# Revit family: BE_24533_de_DE
name_source: partatom
category: Leuchten
units: mm (PartAtom-declared; Revit-internal decimal feet)

## family parameters
Basisbauteil = Fläche
Beim Laden mit Abzugskörper schneiden = Ja
Bemaßung runder Anschluss = Durchmesser verwenden
Gemeinsam genutzt = Nein
Lichtquelle = Nein
Raumberechnungspunkt = Ja
Teiletyp = Normal

## types (4) — shared parameters
AC/DC = AC/DC
Aktualisierung = 2022-05-18T04:00:07
BEGA_Dummy = Nein
Beschreibung = Deckeneinbau-Tiefstrahler
Beschreibung_Sonderanfertigung = Hier können Sie Informationen zur Sonderanfertigung eintragen.
Bestellnummer_Einbaugehäuse = ---
CE_Konformität = ja
ENEC = ja
Einbaugehäuse = Nein
Einbautiefe = 140 mm
Einbauöffnung = 202 mm
Energieeffizienzklasse = LED A++ - A
Farbwiedergabeindex = CRI > 80
Frequenz = 0/50-60 Hz
Gewicht = 2.3 kg
Hersteller = BEGA
Lampe = LED 21.6 W
Lastklassifizierung = Beleuchtung
Lebensdauerkriterien = L70B50 @ 25 °C = 130000 h
Logo = BEGA_Logo.png
Material_03 = BEGA_Oberfläche_Weiss_matt
Material_06 = BEGA_Oberfläche_Edelstahl_gebürstet
Material_09 = BEGA_Glas_klar
Material_13 = BEGA_Kunststoff_matt
Material_15 = BEGA_Leuchtmedium_matt
Material_17 = BEGA_Reflektor
Material_18 = BEGA_Gummi_schwarz
Produktdatenblatt = https://cdn.bega.com
Scheinlast = 0 VA
Schutzart = IP 65
Schutzklasse = II
Sonderanfertigung = Nein
Spannung = 240 V
Strom = 0,6 A
URL = https://www.bega.com
Umgebungstemperatur = 25 °C
zero-valued in all types: Vorgabe-Ansicht

## per-type parameters (varying)
| type | BEGA_IES1 | BEGA_IES2 | Bestellnummer | Farbtemperatur | LED_Modulbezeichnung | Lampenlichtstrom | Leuchtenlichtstrom | M_G | M_W | Modell |
| BEGA_24533_Grafit_K4 | Nein | Ja | 24533K4 | 4000 K | LED-1145/840 | 3400 lm | 1647 lm | Ja | Nein | 24533K4 |
| BEGA_24533_Weiß_K3 | Ja | Nein | 24533WK3 | 3000 K | LED-1145/830 | 3235 lm | 1567 lm | Nein | Ja | 24533WK3 |
| BEGA_24533_Weiß_K4 | Nein | Ja | 24533WK4 | 4000 K | LED-1145/840 | 3400 lm | 1647 lm | Nein | Ja | 24533WK4 |
| BEGA_24533_Grafit_K3 | Ja | Nein | 24533K3 | 3000 K | LED-1145/830 | 3235 lm | 1567 lm | Ja | Nein | 24533K3 |

## geometry (parser evidence)
native form markers: Blend x5, Sweep x11
no freeform markers — native parametric forms only
